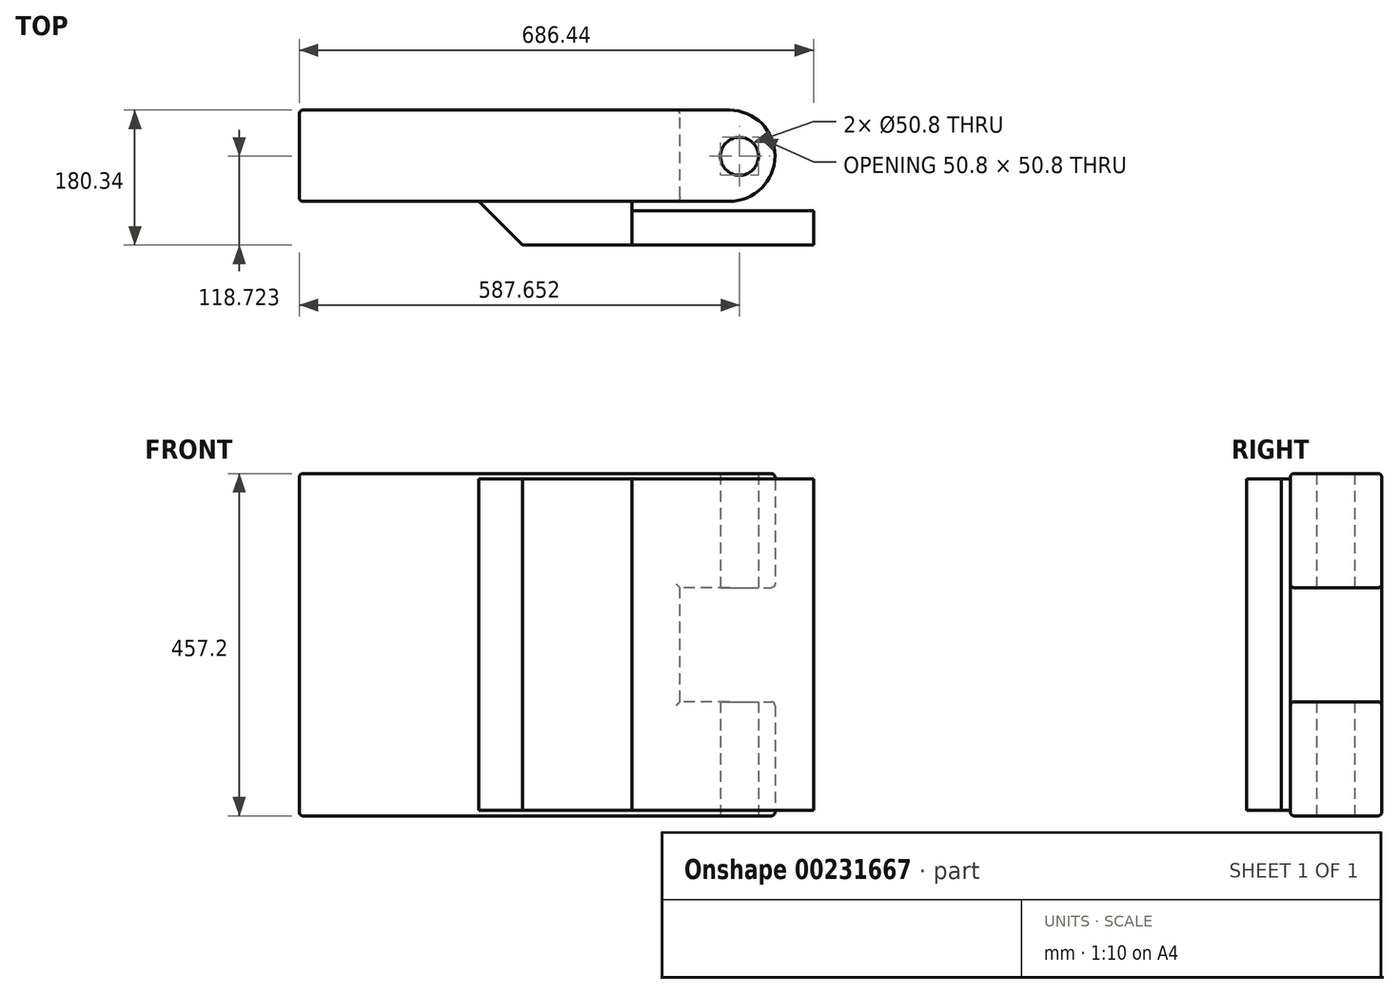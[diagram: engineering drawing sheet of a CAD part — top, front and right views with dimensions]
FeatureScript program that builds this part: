
annotation { "Feature Type Name" : "Feature", "Feature Type Description" : "" }
export const myFeature = defineFeature(function(context is Context, id is Id, definition is map)
    precondition{}
    {
        {
            var Q0;
            Q0=qCreatedBy(makeId("Front.planeOp"),FACE);
            var sketch = newSketch(context, id + "F0", { "sketchPlane" : qUnion([Q0])});
            skLineSegment(sketch, "E0.bottom", {"start": v(-254, -228.6) * mm, "end": v(254, -228.6) * mm});
            skLineSegment(sketch, "E0.top", {"start": v(-254, 228.6) * mm, "end": v(254, 228.6) * mm});
            skLineSegment(sketch, "E0.left", {"start": v(-254, -228.6) * mm, "end": v(-254, 228.6) * mm});
            skLineSegment(sketch, "E0.right", {"start": v(254, -228.6) * mm, "end": v(254, 228.6) * mm});
            skPoint(sketch, "E0.middle", {"position": v(0, 0) * mm});
            skLineSegment(sketch, "E1", {"start": v(254, 228.6) * mm, "end": v(381, 228.6) * mm});
            skLineSegment(sketch, "E2", {"start": v(381, 228.6) * mm, "end": v(381, 76.2) * mm});
            skLineSegment(sketch, "E3", {"start": v(381, 76.2) * mm, "end": v(254, 76.2) * mm});
            skLineSegment(sketch, "E4", {"start": v(254, -228.6) * mm, "end": v(381, -228.6) * mm});
            skLineSegment(sketch, "E5", {"start": v(381, -228.6) * mm, "end": v(381, -76.2) * mm});
            skLineSegment(sketch, "E6", {"start": v(381, -76.2) * mm, "end": v(254, -76.2) * mm});
            skSolve(sketch);
        }
        {
            var Q0;
            Q0 = qSketchRegion(id + "F0", true);
            extrude(context, id + "F1", {"entities" : qUnion([Q0]), "depth" : 121.92 * mm});
        }
        {
            var Q0;
            Q0=makeQuery(id+"F1.opExtrude","CAP_EDGE",EDGE,{"disambiguationData":[OSD([sQuery(id+"F0.wireOp",EDGE,"E2")])],"isStart":false});
            var Q1;
            Q1=makeQuery(id+"F1.opExtrude","CAP_EDGE",EDGE,{"disambiguationData":[OSD([sQuery(id+"F0.wireOp",EDGE,"E2")])],"isStart":true});
            var Q2;
            Q2=makeQuery(id+"F1.opExtrude","CAP_EDGE",EDGE,{"disambiguationData":[OSD([sQuery(id+"F0.wireOp",EDGE,"E5")])],"isStart":false});
            var Q3;
            Q3=makeQuery(id+"F1.opExtrude","CAP_EDGE",EDGE,{"disambiguationData":[OSD([sQuery(id+"F0.wireOp",EDGE,"E5")])],"isStart":true});
            fillet(context, id + "F2", {"entities" : qUnion([Q0, Q1, Q2, Q3]), "radius" : 60.96 * mm, "tangentPropagation" : true, "allowEdgeOverflow" : false});
        }
        {
            var Q0;
            Q0=makeQuery(id+"F1.opExtrude","CAP_FACE",FACE,{"disambiguationData":[OSD([sQuery(id+"F0.wireOp",EDGE,"E0.bottom"),sQuery(id+"F0.wireOp",EDGE,"E0.top"),sQuery(id+"F0.wireOp",EDGE,"E0.left"),sQuery(id+"F0.wireOp",EDGE,"E0.right"),sQuery(id+"F0.wireOp",EDGE,"E1"),sQuery(id+"F0.wireOp",EDGE,"E2"),sQuery(id+"F0.wireOp",EDGE,"E3"),sQuery(id+"F0.wireOp",EDGE,"E4"),sQuery(id+"F0.wireOp",EDGE,"E5"),sQuery(id+"F0.wireOp",EDGE,"E6")])],"isStart":true});
            fillet(context, id + "F3", {"entities" : qUnion([Q0]), "radius" : 5.08 * mm, "tangentPropagation" : true, "allowEdgeOverflow" : false});
        }
        {
            var Q0;
            Q0=makeQuery(id+"F1.opExtrude","CAP_FACE",FACE,{"disambiguationData":[OSD([sQuery(id+"F0.wireOp",EDGE,"E0.bottom"),sQuery(id+"F0.wireOp",EDGE,"E0.top"),sQuery(id+"F0.wireOp",EDGE,"E0.left"),sQuery(id+"F0.wireOp",EDGE,"E0.right"),sQuery(id+"F0.wireOp",EDGE,"E1"),sQuery(id+"F0.wireOp",EDGE,"E2"),sQuery(id+"F0.wireOp",EDGE,"E3"),sQuery(id+"F0.wireOp",EDGE,"E4"),sQuery(id+"F0.wireOp",EDGE,"E5"),sQuery(id+"F0.wireOp",EDGE,"E6")])],"isStart":false});
            fillet(context, id + "F4", {"entities" : qUnion([Q0]), "radius" : 5.08 * mm, "tangentPropagation" : true, "allowEdgeOverflow" : false});
        }
        {
            var Q0;
            Q0=makeQuery(id+"F1.opExtrude","SWEPT_FACE",FACE,{"disambiguationData":[OSD([sQuery(id+"F0.wireOp",EDGE,"E0.bottom"),sQuery(id+"F0.wireOp",EDGE,"E4")])]});
            cPlane(context, id + "F5", {"entities" : qUnion([Q0]), "cplaneType" : CPlaneType.OFFSET, "offset" : 25.4 * mm, "width" : 152.4 * mm, "height" : 152.4 * mm});
        }
        {
            var Q0;
            Q0=qCreatedBy(id+"F5.planeOp",FACE);
            var sketch = newSketch(context, id + "F6", { "sketchPlane" : qUnion([Q0])});
            skLineSegment(sketch, "E7", {"start": v(440.3, -57.47) * mm, "end": v(440.3, 180.7) * mm, "construction": true});
            skLineSegment(sketch, "E8", {"start": v(440.3, 180.7) * mm, "end": v(440.3, 61.62) * mm, "construction": true});
            skLineSegment(sketch, "E9", {"start": v(440.3, 61.62) * mm, "end": v(182.93, 61.62) * mm, "construction": true});
            skPoint(sketch, "E10", {"position": v(333.65, 61.62) * mm});
            skSolve(sketch);
        }
        {
            var Q0;
            Q0=makeQuery(id+"F1.opExtrude","CAP_FACE",FACE,{"disambiguationData":[OSD([sQuery(id+"F0.wireOp",EDGE,"E0.bottom"),sQuery(id+"F0.wireOp",EDGE,"E0.top"),sQuery(id+"F0.wireOp",EDGE,"E0.left"),sQuery(id+"F0.wireOp",EDGE,"E0.right"),sQuery(id+"F0.wireOp",EDGE,"E1"),sQuery(id+"F0.wireOp",EDGE,"E2"),sQuery(id+"F0.wireOp",EDGE,"E3"),sQuery(id+"F0.wireOp",EDGE,"E4"),sQuery(id+"F0.wireOp",EDGE,"E5"),sQuery(id+"F0.wireOp",EDGE,"E6")])],"isStart":false});
            cPlane(context, id + "F7", {"entities" : qUnion([Q0]), "cplaneType" : CPlaneType.OFFSET, "offset" : 25.4 * mm, "oppositeDirection" : true, "width" : 152.4 * mm, "height" : 152.4 * mm});
        }
        {
            var Q0;
            Q0=qCreatedBy(id+"F7.planeOp",FACE);
            var sketch = newSketch(context, id + "F8", { "sketchPlane" : qUnion([Q0])});
            skLineSegment(sketch, "E11.bottom", {"start": v(43.82, 221.3) * mm, "end": v(190.1, 221.3) * mm});
            skLineSegment(sketch, "E11.top", {"start": v(43.82, -221.3) * mm, "end": v(190.1, -221.3) * mm});
            skLineSegment(sketch, "E11.left", {"start": v(43.82, 221.3) * mm, "end": v(43.82, -221.3) * mm});
            skLineSegment(sketch, "E11.right", {"start": v(190.1, 221.3) * mm, "end": v(190.1, -221.3) * mm});
            skPoint(sketch, "E11.middle", {"position": v(116.96, 0) * mm});
            skSolve(sketch);
        }
        {
            var Q0;
            Q0 = qSketchRegion(id + "F8", true);
            extrude(context, id + "F9", {"entities" : qUnion([Q0]), "operationType" : NewBodyOperationType.ADD, "depth" : 83.82 * mm});
        }
        {
            var Q0;
            Q0=makeQuery(id+"F9.opExtrude","SWEPT_FACE",FACE,{"disambiguationData":[OSD([sQuery(id+"F8.wireOp",EDGE,"E11.left")])]});
            cPlane(context, id + "F10", {"entities" : qUnion([Q0]), "cplaneType" : CPlaneType.OFFSET, "offset" : 25.4 * mm, "oppositeDirection" : true, "width" : 152.4 * mm, "height" : 152.4 * mm});
        }
        {
            var Q0;
            Q0=makeQuery(id+"F9.boolean.opBoolean","INTERSECT",EDGE,{"derivedFrom":[makeQuery(id+"F1.opExtrude","CAP_FACE",FACE,{"disambiguationData":[OSD([sQuery(id+"F0.wireOp",EDGE,"E0.bottom"),sQuery(id+"F0.wireOp",EDGE,"E0.top"),sQuery(id+"F0.wireOp",EDGE,"E0.left"),sQuery(id+"F0.wireOp",EDGE,"E0.right"),sQuery(id+"F0.wireOp",EDGE,"E1"),sQuery(id+"F0.wireOp",EDGE,"E2"),sQuery(id+"F0.wireOp",EDGE,"E3"),sQuery(id+"F0.wireOp",EDGE,"E4"),sQuery(id+"F0.wireOp",EDGE,"E5"),sQuery(id+"F0.wireOp",EDGE,"E6")])],"isStart":false}),makeQuery(id+"F9.opExtrude","SWEPT_FACE",FACE,{"disambiguationData":[OSD([sQuery(id+"F8.wireOp",EDGE,"E11.left")])]})]});
            chamfer(context, id + "F11", {"entities" : qUnion([Q0]), "width" : 58.42 * mm, "tangentPropagation" : true});
        }
        {
            var Q0;
            Q0=qCreatedBy(id+"F10.planeOp",FACE);
            var sketch = newSketch(context, id + "F12", { "sketchPlane" : qUnion([Q0])});
            skPoint(sketch, "E12.top.end.orphan", {"position": v(134.21, 51.57) * mm});
            skPoint(sketch, "E13.top.end.orphan", {"position": v(134.21, -49.7) * mm});
            skLineSegment(sketch, "E14.bottom", {"start": v(180.22, 221.19) * mm, "end": v(134.07, 221.19) * mm});
            skLineSegment(sketch, "E14.top", {"start": v(180.22, -221.12) * mm, "end": v(134.07, -221.12) * mm});
            skLineSegment(sketch, "E14.left", {"start": v(180.22, 221.19) * mm, "end": v(180.22, -221.12) * mm});
            skLineSegment(sketch, "E14.right", {"start": v(134.07, 221.19) * mm, "end": v(134.07, -221.12) * mm});
            skSolve(sketch);
        }
        {
            var Q0;
            Q0=sQuery(id+"F6.wireOp",VERTEX,"E10");
            var Q1;
            Q1=makeQuery(id+"F1.opExtrude","SWEPT_BODY",BODY,{"disambiguationData":[OSD([sQuery(id+"F0.wireOp",EDGE,"E0.bottom"),sQuery(id+"F0.wireOp",EDGE,"E0.top"),sQuery(id+"F0.wireOp",EDGE,"E0.left"),sQuery(id+"F0.wireOp",EDGE,"E0.right"),sQuery(id+"F0.wireOp",EDGE,"E1"),sQuery(id+"F0.wireOp",EDGE,"E2"),sQuery(id+"F0.wireOp",EDGE,"E3"),sQuery(id+"F0.wireOp",EDGE,"E4"),sQuery(id+"F0.wireOp",EDGE,"E5"),sQuery(id+"F0.wireOp",EDGE,"E6")])]});
            hole(context, id + "F13", {"style" : HoleStyle.SIMPLE, "endStyle" : HoleEndStyle.THROUGH, "holeDiameter" : 50.8 * mm, "locations" : qUnion([Q0]), "scope" : qUnion([Q1]), "isTappedThrough" : true});
        }
        {
            var Q0;
            Q0 = qSketchRegion(id + "F12", true);
            extrude(context, id + "F14", {"entities" : qUnion([Q0]), "operationType" : NewBodyOperationType.ADD, "oppositeDirection" : true, "depth" : 363.22 * mm});
        }
    });
